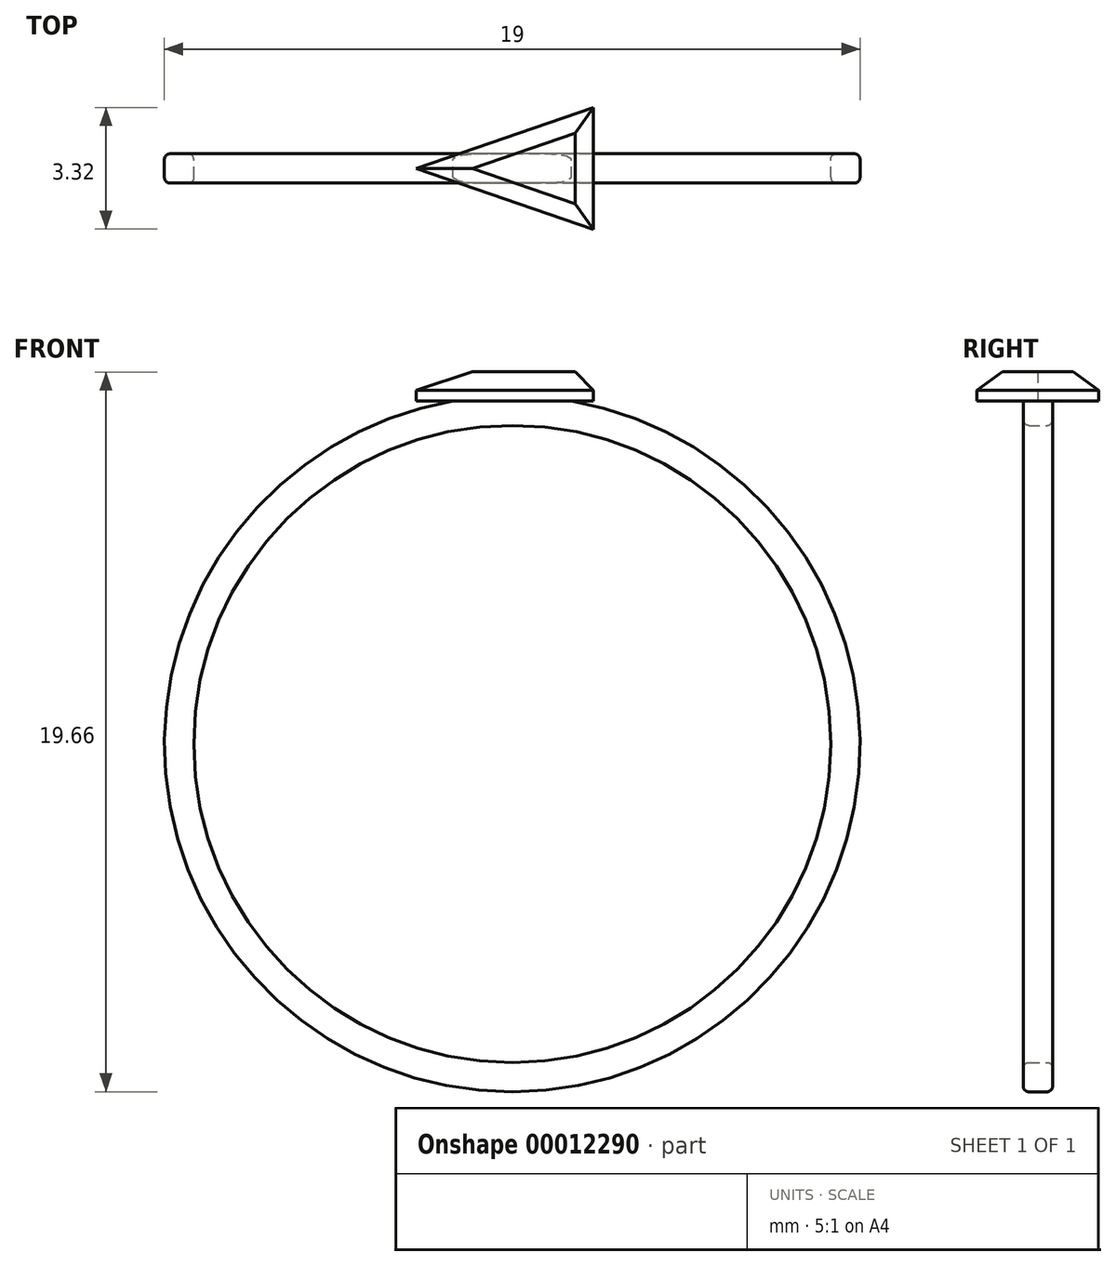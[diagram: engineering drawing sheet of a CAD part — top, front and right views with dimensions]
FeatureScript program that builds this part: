
annotation { "Feature Type Name" : "Feature", "Feature Type Description" : "" }
export const myFeature = defineFeature(function(context is Context, id is Id, definition is map)
    precondition{}
    {
        {
            var Q0;
            Q0=qCreatedBy(makeId("Front.planeOp"),FACE);
            var sketch = newSketch(context, id + "F0", { "sketchPlane" : qUnion([Q0])});
            skCircle(sketch, "E0", {"center": v(0, 0) * mm, "radius": 8.7 * mm});
            skCircle(sketch, "E1", {"center": v(0, 0) * mm, "radius": 9.5 * mm});
            skLineSegment(sketch, "E2", {"start": v(-1.62, 9.36) * mm, "end": v(1.62, 9.36) * mm});
            skLineSegment(sketch, "E3", {"start": v(1.62, 9.36) * mm, "end": v(0, 0) * mm});
            skLineSegment(sketch, "E4", {"start": v(-1.62, 9.36) * mm, "end": v(0, 0) * mm});
            skSolve(sketch);
        }
        {
            var Q0;
            {var subQ1=sQuery(id+"F0.wireOp",EDGE,"E0");var subQ6=sQuery(id+"F0.wireOp",EDGE,"E3");var subQ7=makeQuery(id+"F0.imprint","INTERSECT",VERTEX,{"derivedFrom":[subQ1,subQ6]});Q0=makeQuery(id+"F0.imprint","IMPRINT",FACE,{"disambiguationData":[TD([[makeQuery(id+"F0.imprint","IMPRINT",EDGE,{"disambiguationData":[TD([[subQ7,1.0]])],"derivedFrom":subQ1}),-1.0]])]});}
            var Q1;
            {var subQ4=sQuery(id+"F0.wireOp",EDGE,"E2");Q1=makeQuery(id+"F0.imprint","IMPRINT",FACE,{"disambiguationData":[TD([[makeQuery(id+"F0.imprint","IMPRINT",EDGE,{"derivedFrom":subQ4}),-1.0]])]});}
            extrude(context, id + "F1", {"entities" : qUnion([Q0, Q1]), "depth" : .4 * mm});
        }
        {
            var Q0;
            {var subQ1=sQuery(id+"F0.wireOp",EDGE,"E0");var subQ6=sQuery(id+"F0.wireOp",EDGE,"E3");var subQ7=makeQuery(id+"F0.imprint","INTERSECT",VERTEX,{"derivedFrom":[subQ1,subQ6]});Q0=makeQuery(id+"F0.imprint","IMPRINT",FACE,{"disambiguationData":[TD([[makeQuery(id+"F0.imprint","IMPRINT",EDGE,{"disambiguationData":[TD([[subQ7,1.0]])],"derivedFrom":subQ1}),-1.0]])]});}
            var Q1;
            {var subQ4=sQuery(id+"F0.wireOp",EDGE,"E2");Q1=makeQuery(id+"F0.imprint","IMPRINT",FACE,{"disambiguationData":[TD([[makeQuery(id+"F0.imprint","IMPRINT",EDGE,{"derivedFrom":subQ4}),-1.0]])]});}
            extrude(context, id + "F2", {"entities" : qUnion([Q0, Q1]), "operationType" : NewBodyOperationType.ADD, "oppositeDirection" : true, "depth" : .4 * mm});
        }
        {
            var Q0;
            {var subQ0=sQuery(id+"F0.wireOp",EDGE,"E2");Q0=makeQuery(id+"F2.boolean.opBoolean","MERGE",FACE,{"derivedFrom":[makeQuery(id+"F1.opExtrude","SWEPT_FACE",FACE,{"disambiguationData":[OSD([subQ0])]}),makeQuery(id+"F2.opExtrude","SWEPT_FACE",FACE,{"disambiguationData":[OSD([subQ0])]})]});}
            var sketch = newSketch(context, id + "F3", { "sketchPlane" : qUnion([Q0])});
            skLineSegment(sketch, "E5", {"start": v(2.22, -1.66) * mm, "end": v(-2.62, 0) * mm});
            skLineSegment(sketch, "E6", {"start": v(-2.62, 0) * mm, "end": v(2.22, 1.66) * mm});
            skLineSegment(sketch, "E7", {"start": v(2.22, -1.66) * mm, "end": v(2.22, 1.66) * mm});
            skSolve(sketch);
        }
        {
            var Q0;
            Q0=makeQuery(id+"F2.opExtrude","CAP_EDGE",EDGE,{"disambiguationData":[OSD([sQuery(id+"F0.wireOp",EDGE,"E1")])],"isStart":false});
            var Q1;
            Q1=makeQuery(id+"F2.opExtrude","CAP_EDGE",EDGE,{"disambiguationData":[OSD([sQuery(id+"F0.wireOp",EDGE,"E0")])],"isStart":false});
            var Q2;
            Q2=makeQuery(id+"F1.opExtrude","CAP_EDGE",EDGE,{"disambiguationData":[OSD([sQuery(id+"F0.wireOp",EDGE,"E0")])],"isStart":false});
            var Q3;
            Q3=makeQuery(id+"F1.opExtrude","CAP_EDGE",EDGE,{"disambiguationData":[OSD([sQuery(id+"F0.wireOp",EDGE,"E1")])],"isStart":false});
            fillet(context, id + "F4", {"entities" : qUnion([Q0, Q1, Q2, Q3]), "radius" : .15 * mm, "tangentPropagation" : true, "allowEdgeOverflow" : false});
        }
        {
            var Q0;
            Q0 = qSketchRegion(id + "F3", true);
            extrude(context, id + "F5", {"entities" : qUnion([Q0]), "operationType" : NewBodyOperationType.ADD, "depth" : .8 * mm});
        }
        {
            var Q0;
            Q0=makeQuery(id+"F5.opExtrude","CAP_FACE",FACE,{"disambiguationData":[OSD([sQuery(id+"F3.wireOp",EDGE,"E5"),sQuery(id+"F3.wireOp",EDGE,"E6"),sQuery(id+"F3.wireOp",EDGE,"E7")])],"isStart":false});
            chamfer(context, id + "F6", {"entities" : qUnion([Q0]), "width" : .5 * mm, "tangentPropagation" : true});
        }
    });
